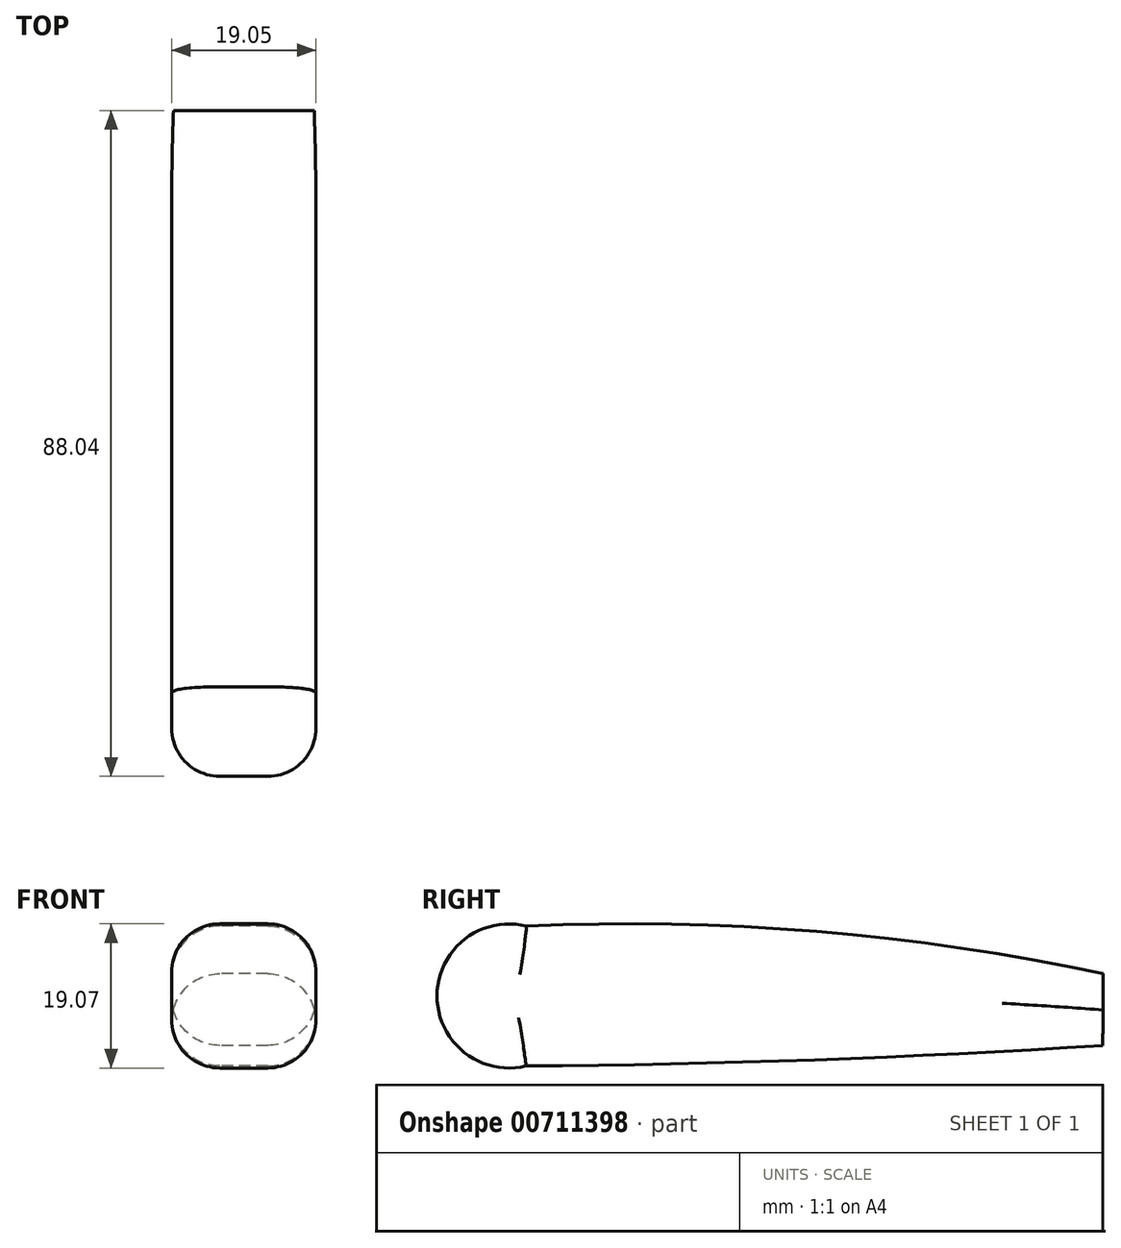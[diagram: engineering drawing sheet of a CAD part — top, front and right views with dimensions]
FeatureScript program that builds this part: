
annotation { "Feature Type Name" : "Feature", "Feature Type Description" : "" }
export const myFeature = defineFeature(function(context is Context, id is Id, definition is map)
    precondition{}
    {
        {
            var Q0;
            Q0=qCreatedBy(makeId("Right.planeOp"),FACE);
            var sketch = newSketch(context, id + "F0", { "sketchPlane" : qUnion([Q0])});
            skCircle(sketch, "E0", {"center": v(-84.5, 0) * mm, "radius": 9.53 * mm});
            skArc(sketch, "E1", {"start": v(-5.99, 2.95) * mm, "mid": v(-43.9, 8.51) * mm, "end": v(-82.19, 9.24) * mm});
            skArc(sketch, "E2", {"start": v(-82.26, -9.26) * mm, "mid": v(-44.14, -8.45) * mm, "end": v(-6.06, -6.54) * mm});
            skLineSegment(sketch, "E3", {"start": v(-5.99, 2.95) * mm, "end": v(-6.06, -6.54) * mm});
            skSolve(sketch);
        }
        {
            var Q0;
            {var subQ0=sQuery(id+"F0.wireOp",EDGE,"E0");var subQ1=makeQuery(id+"F0.imprint","INTERSECT",VERTEX,{"derivedFrom":[subQ0,sQuery(id+"F0.wireOp",EDGE,"E1")]});Q0=makeQuery(id+"F0.imprint","IMPRINT",FACE,{"disambiguationData":[TD([[makeQuery(id+"F0.imprint","IMPRINT",EDGE,{"disambiguationData":[TD([[subQ1,-1.0]])],"derivedFrom":subQ0}),1.0]])]});}
            var Q1;
            {var subQ4=sQuery(id+"F0.wireOp",EDGE,"E1");Q1=makeQuery(id+"F0.imprint","IMPRINT",FACE,{"disambiguationData":[TD([[makeQuery(id+"F0.imprint","IMPRINT",EDGE,{"derivedFrom":subQ4}),1.0]])]});}
            var Q2;
            {var subQ5=sQuery(id+"F0.wireOp",EDGE,"qaeUne9z-xtif-f2jW-rhNB-IM0dlZ6w0C06.right");Q2=makeQuery(id+"F0.imprint","IMPRINT",FACE,{"disambiguationData":[TD([[makeQuery(id+"F0.imprint","IMPRINT",EDGE,{"derivedFrom":subQ5}),-1.0]])]});}
            var Q3;
            {var subQ5=sQuery(id+"F0.wireOp",EDGE,"qaeUne9z-xtif-f2jW-rhNB-IM0dlZ6w0C06.left");Q3=makeQuery(id+"F0.imprint","IMPRINT",FACE,{"disambiguationData":[TD([[makeQuery(id+"F0.imprint","IMPRINT",EDGE,{"derivedFrom":subQ5}),1.0]])]});}
            var Q4;
            {var subQ5=sQuery(id+"F0.wireOp",EDGE,"XR0LLpR2-xg4K-DRgD-4if0-bppmhXIHbowb.right");Q4=makeQuery(id+"F0.imprint","IMPRINT",FACE,{"disambiguationData":[TD([[makeQuery(id+"F0.imprint","IMPRINT",EDGE,{"derivedFrom":subQ5}),-1.0]])]});}
            var Q5;
            {var subQ5=sQuery(id+"F0.wireOp",EDGE,"XR0LLpR2-xg4K-DRgD-4if0-bppmhXIHbowb.left");Q5=makeQuery(id+"F0.imprint","IMPRINT",FACE,{"disambiguationData":[TD([[makeQuery(id+"F0.imprint","IMPRINT",EDGE,{"derivedFrom":subQ5}),1.0]])]});}
            extrude(context, id + "F1", {"entities" : qUnion([Q0, Q1, Q2, Q3, Q4, Q5]), "depth" : 19.05 * mm, "offsetDistance" : 25.4 * mm});
        }
        {
            var Q0;
            Q0=makeQuery(id+"F1.opExtrude","CAP_EDGE",EDGE,{"disambiguationData":[OSD([sQuery(id+"F0.wireOp",EDGE,"E0")])],"isStart":false});
            var Q1;
            Q1=makeQuery(id+"F1.opExtrude","CAP_EDGE",EDGE,{"disambiguationData":[OSD([sQuery(id+"F0.wireOp",EDGE,"E1")])],"isStart":false});
            var Q2;
            Q2=makeQuery(id+"F1.opExtrude","CAP_EDGE",EDGE,{"disambiguationData":[OSD([sQuery(id+"F0.wireOp",EDGE,"E2")])],"isStart":false});
            var Q3;
            Q3=makeQuery(id+"F1.opExtrude","CAP_EDGE",EDGE,{"disambiguationData":[OSD([sQuery(id+"F0.wireOp",EDGE,"E0")])],"isStart":true});
            var Q4;
            Q4=makeQuery(id+"F1.opExtrude","CAP_EDGE",EDGE,{"disambiguationData":[OSD([sQuery(id+"F0.wireOp",EDGE,"E1")])],"isStart":true});
            var Q5;
            Q5=makeQuery(id+"F1.opExtrude","CAP_EDGE",EDGE,{"disambiguationData":[OSD([sQuery(id+"F0.wireOp",EDGE,"E2")])],"isStart":true});
            fillet(context, id + "F2", {"entities" : qUnion([Q0, Q1, Q2, Q3, Q4, Q5]), "radius" : 6.35 * mm, "tangentPropagation" : true, "allowEdgeOverflow" : false});
        }
    });
